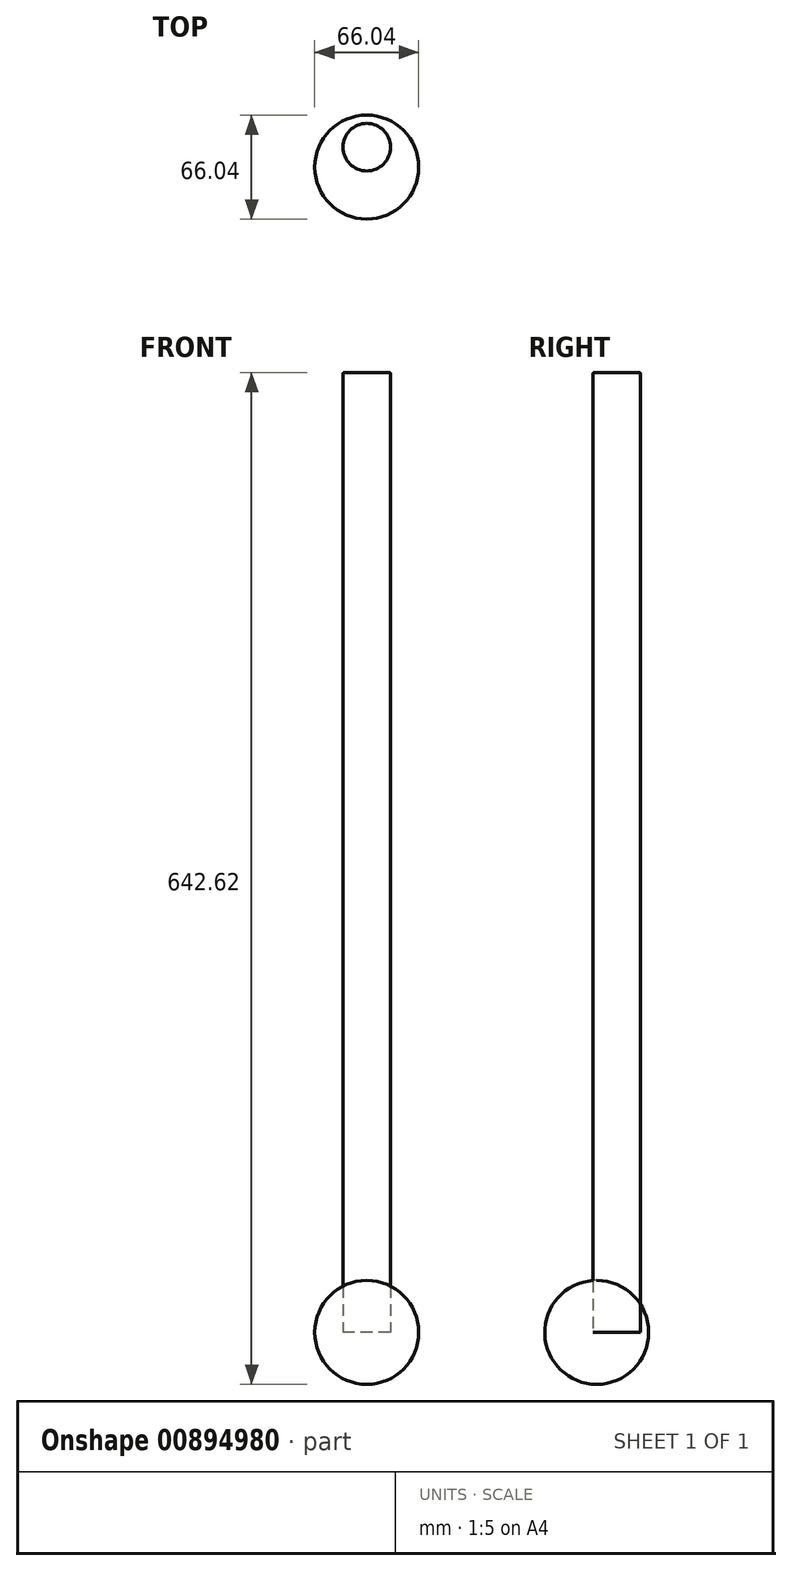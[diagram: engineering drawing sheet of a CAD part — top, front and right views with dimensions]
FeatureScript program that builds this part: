
annotation { "Feature Type Name" : "Feature", "Feature Type Description" : "" }
export const myFeature = defineFeature(function(context is Context, id is Id, definition is map)
    precondition{}
    {
        {
            var Q0;
            Q0=qCreatedBy(makeId("Top.planeOp"),FACE);
            var sketch = newSketch(context, id + "F0", { "sketchPlane" : qUnion([Q0])});
            skCircle(sketch, "E0", {"center": v(0, 0) * mm, "radius": 15.11 * mm});
            skSolve(sketch);
        }
        {
            var Q0;
            Q0=makeQuery(id+"F0.imprint","IMPRINT",FACE,{"disambiguationData":[TD([[makeQuery(id+"F0.imprint","IMPRINT",EDGE,{"derivedFrom":sQuery(id+"F0.wireOp",EDGE,"E0")}),1.0]])]});
            extrude(context, id + "F1", {"entities" : qUnion([Q0]), "depth" : 609.6 * mm, "offsetDistance" : 25.4 * mm});
        }
        {
            var Q0;
            Q0=makeQuery(id+"F1.opExtrude","CAP_EDGE",EDGE,{"disambiguationData":[OSD([sQuery(id+"F0.wireOp",EDGE,"E0")])],"isStart":false});
            fillet(context, id + "F2", {"entities" : qUnion([Q0]), "radius" : 0.64 * mm, "tangentPropagation" : true, "allowEdgeOverflow" : false});
        }
        {
            var Q0;
            Q0=qCreatedBy(makeId("Right.planeOp"),FACE);
            var sketch = newSketch(context, id + "F3", { "sketchPlane" : qUnion([Q0])});
            skArc(sketch, "E1", {"start": v(0, -41.28) * mm, "mid": v(41.28, 0) * mm, "end": v(0, 41.28) * mm});
            skLineSegment(sketch, "E2", {"start": v(0, 0) * mm, "end": v(0, 41.28) * mm, "construction": true});
            skLineSegment(sketch, "E3", {"start": v(0, 0) * mm, "end": v(0, -41.28) * mm, "construction": true});
            skSolve(sketch);
        }
        {
            var Q0;
            Q0=sQuery(id+"F3.wireOp",EDGE,"E1");
            var Q1;
            Q1=sQuery(id+"F3.wireOp",EDGE,"E3");
            revolve(context, id + "F4", {"bodyType" : ToolBodyType.SURFACE, "surfaceOperationType" : NewSurfaceOperationType.NEW, "surfaceEntities" : qUnion([Q0]), "axis" : qUnion([Q1]), "revolveType" : RevolveType.FULL});
        }
        {
            var Q0;
            Q0=qCreatedBy(makeId("Front.planeOp"),FACE);
            cPlane(context, id + "F5", {"entities" : qUnion([Q0]), "cplaneType" : CPlaneType.OFFSET, "offset" : 12.7 * mm, "width" : 152.4 * mm, "height" : 152.4 * mm});
        }
        {
            var Q0;
            Q0=qCreatedBy(id+"F5.planeOp",FACE);
            var sketch = newSketch(context, id + "F6", { "sketchPlane" : qUnion([Q0])});
            skArc(sketch, "E4", {"start": v(0, -33.02) * mm, "mid": v(33.02, 0) * mm, "end": v(0, 33.02) * mm});
            skLineSegment(sketch, "E5", {"start": v(0, -33.02) * mm, "end": v(0, 33.02) * mm});
            skSolve(sketch);
        }
        {
            var Q0;
            Q0 = qSketchRegion(id + "F6", true);
            var Q1;
            Q1=sQuery(id+"F6.wireOp",EDGE,"E5");
            revolve(context, id + "F7", {"surfaceOperationType" : NewSurfaceOperationType.NEW, "entities" : qUnion([Q0]), "axis" : qUnion([Q1]), "revolveType" : RevolveType.FULL});
        }
    });
